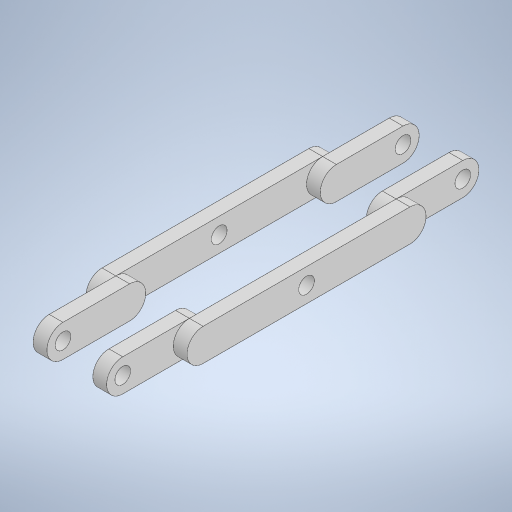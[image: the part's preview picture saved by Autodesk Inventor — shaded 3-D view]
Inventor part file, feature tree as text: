
AUTODESK INVENTOR PART (.ipt)
format: ipt  version: 2024.3 (Build 283343000, 343)  size: 305,664 bytes
history: native  units: mm
features: extrude x4, sketch x3, hole x2
ambient origin geometry x8: Origin, YZ Plane, XZ Plane, XY Plane, X Axis, Y Axis, Z Axis, Center Point
bodies: Body1 (feature_tree)
feature tree (9):
  sketch  "Sketch1"  dims[d17=5.0mm d18=81.0mm]
  extrude  "Extrusión3"  Depth=81.0mm
  extrude  "Extrusión4"  Depth=7.0mm
  extrude  "Extrusión5"  Depth=16.0mm TaperAngle=0.0deg
  extrude  "Extrusión6"  Depth=8.0mm
  hole  "Agujero1"  [1 undecoded]
  hole  "Agujero2"  [1 undecoded]
  sketch  "Boceto2"  dims[d19=3.0mm d20=7.0mm]
  sketch  "Boceto3"  dims[d21=22.0mm d22=0.0mm d23=16.0mm d24=0.0mm d25=3.4mm d26=6.0mm d27=6.3mm d28=2.0mm d29=90.0deg d30=8.0mm d31=20.594885mm d32=45.0mm d33=16.0mm d34=0.0mm d35=10.0mm d36=0.0mm d37=3.4mm d38=6.0mm d39=6.3mm d40=2.0mm d41=90.0deg d42=8.0mm d43=20.594885mm]
note: 2 required parameter values undecoded (feature->parameter linkage not recoverable at this tier; creation-order binding heuristic only, values carry confidence <= 0.55)
